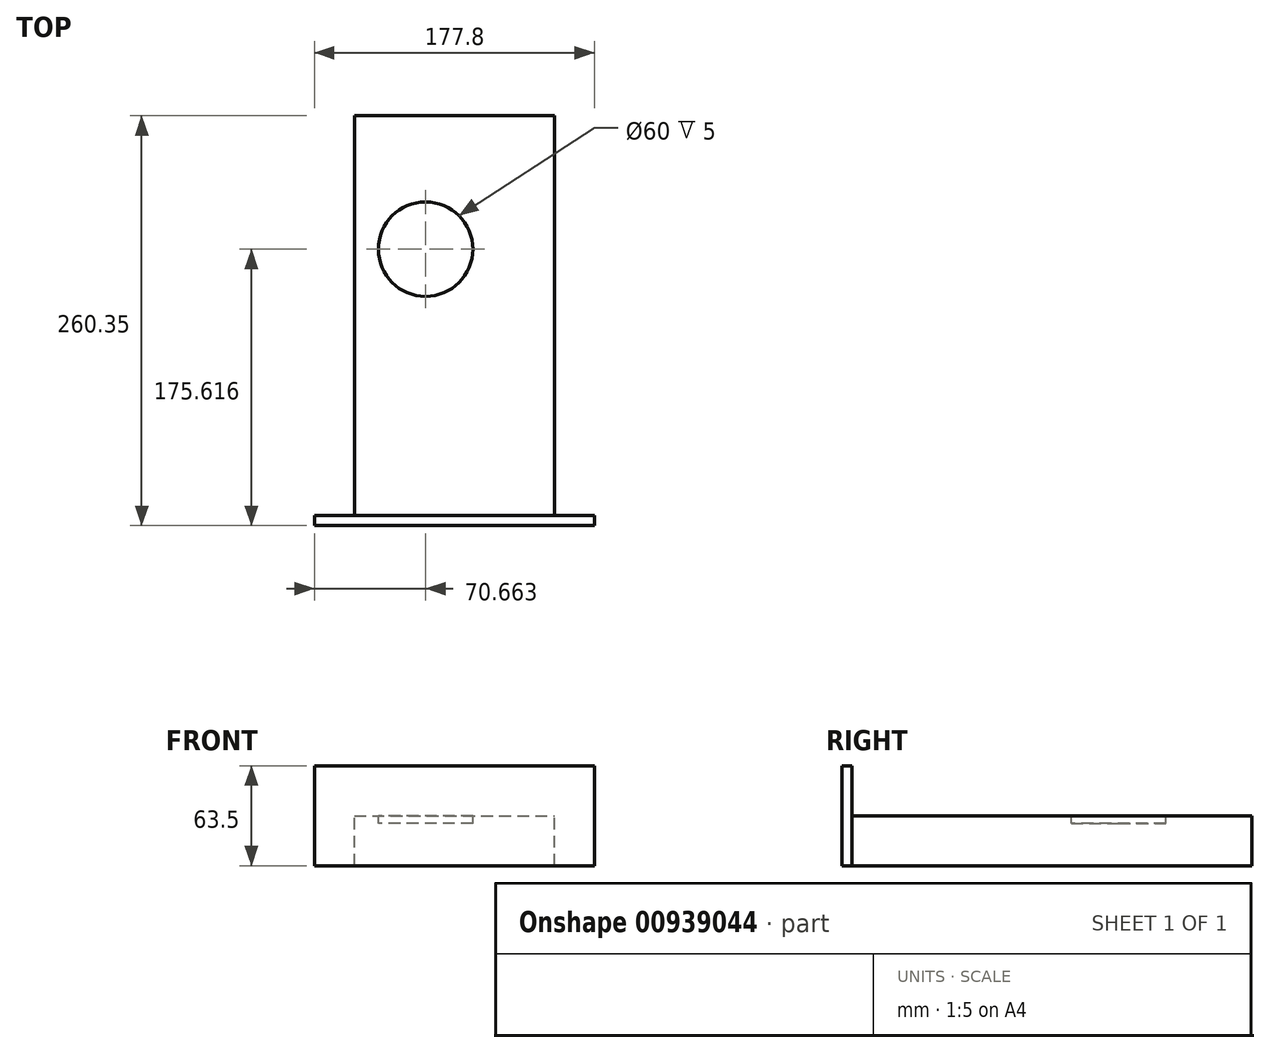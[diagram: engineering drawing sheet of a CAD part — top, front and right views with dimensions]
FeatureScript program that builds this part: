
annotation { "Feature Type Name" : "Feature", "Feature Type Description" : "" }
export const myFeature = defineFeature(function(context is Context, id is Id, definition is map)
    precondition{}
    {
        {
            var Q0;
            Q0=qCreatedBy(makeId("Front.planeOp"),FACE);
            var sketch = newSketch(context, id + "F0", { "sketchPlane" : qUnion([Q0])});
            skLineSegment(sketch, "E0.bottom", {"start": v(88.9, 31.75) * mm, "end": v(-88.9, 31.75) * mm});
            skLineSegment(sketch, "E0.top", {"start": v(88.9, -31.75) * mm, "end": v(-88.9, -31.75) * mm});
            skLineSegment(sketch, "E0.left", {"start": v(88.9, 31.75) * mm, "end": v(88.9, -31.75) * mm});
            skLineSegment(sketch, "E0.right", {"start": v(-88.9, 31.75) * mm, "end": v(-88.9, -31.75) * mm});
            skPoint(sketch, "E0.middle", {"position": v(0, 0) * mm});
            skSolve(sketch);
        }
        {
            var Q0;
            Q0 = qSketchRegion(id + "F0", true);
            extrude(context, id + "F1", {"entities" : qUnion([Q0]), "depth" : 6.35 * mm, "offsetDistance" : 25.4 * mm});
        }
        {
            var Q0;
            Q0=makeQuery(id+"F1.opExtrude","CAP_FACE",FACE,{"disambiguationData":[OSD([sQuery(id+"F0.wireOp",EDGE,"E0.bottom"),sQuery(id+"F0.wireOp",EDGE,"E0.top"),sQuery(id+"F0.wireOp",EDGE,"E0.left"),sQuery(id+"F0.wireOp",EDGE,"E0.right")])],"isStart":true});
            var sketch = newSketch(context, id + "F2", { "sketchPlane" : qUnion([Q0])});
            skLineSegment(sketch, "E1", {"start": v(88.9, -31.75) * mm, "end": v(63.5, -31.75) * mm});
            skLineSegment(sketch, "E2.bottom", {"start": v(63.5, -31.75) * mm, "end": v(-63.5, -31.75) * mm});
            skLineSegment(sketch, "E2.top", {"start": v(63.5, 0) * mm, "end": v(-63.5, 0) * mm});
            skLineSegment(sketch, "E2.left", {"start": v(63.5, -31.75) * mm, "end": v(63.5, 0) * mm});
            skLineSegment(sketch, "E2.right", {"start": v(-63.5, -31.75) * mm, "end": v(-63.5, 0) * mm});
            skSolve(sketch);
        }
        {
            var Q0;
            Q0 = qSketchRegion(id + "F2", true);
            extrude(context, id + "F3", {"entities" : qUnion([Q0]), "operationType" : NewBodyOperationType.ADD, "depth" : 254 * mm, "offsetDistance" : 25.4 * mm});
        }
        {
            var Q0;
            Q0=makeQuery(id+"F3.opExtrude","SWEPT_FACE",FACE,{"disambiguationData":[OSD([sQuery(id+"F2.wireOp",EDGE,"E2.top")])]});
            var sketch = newSketch(context, id + "F4", { "sketchPlane" : qUnion([Q0])});
            skLineSegment(sketch, "E3", {"start": v(63.5, 254) * mm, "end": v(63.5, 169.27) * mm});
            skLineSegment(sketch, "E4", {"start": v(63.5, 169.27) * mm, "end": v(-18.24, 169.27) * mm});
            skCircle(sketch, "E5", {"center": v(-18.24, 169.27) * mm, "radius": 30 * mm});
            skSolve(sketch);
        }
        {
            var Q0;
            Q0 = qSketchRegion(id + "F4", true);
            extrude(context, id + "F5", {"entities" : qUnion([Q0]), "operationType" : NewBodyOperationType.REMOVE, "oppositeDirection" : true, "depth" : 5 * mm, "offsetDistance" : 25.4 * mm});
        }
    });
